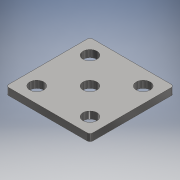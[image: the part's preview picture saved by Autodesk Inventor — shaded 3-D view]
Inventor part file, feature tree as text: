
AUTODESK INVENTOR PART (.ipt)
format: ipt  version: 2018 (Build 220112000, 112)  size: 126,976 bytes
history: native  units: mm
features: reference x4, other x4, sketch x2, extrude x1, fillet x1, hole x1
ambient origin geometry x8: Origin, YZ Plane, XZ Plane, XY Plane, X Axis, Y Axis, Z Axis, Center Point
bodies: Body1 (feature_tree)
feature tree (13):
  extrude  "Estrusione2"  Depth=60.0mm
  fillet  "Raccordo2"  Radius=60.0mm
  hole  "Foro1"  [1 undecoded]
  sketch  "Schizzo1"
  sketch  "Schizzo3"
  reference  "Riferimento1"
  reference  "Riferimento2"
  reference  "Riferimento3"
  reference  "Riferimento4"
  other  "<userpath>\no-brim\Meccanica\Progetto Inventor no-brim\Assiemi\Assieme 2 - Taglio.iam"
  other  "Assieme 2 - Taglio.iam"
  other  "536288 ADN-40-100-I-P-A---(0):2"
  other  "536288 ADN-100-P---(Z):1"
note: 1 required parameter value undecoded (feature->parameter linkage not recoverable at this tier; creation-order binding heuristic only, values carry confidence <= 0.55)
